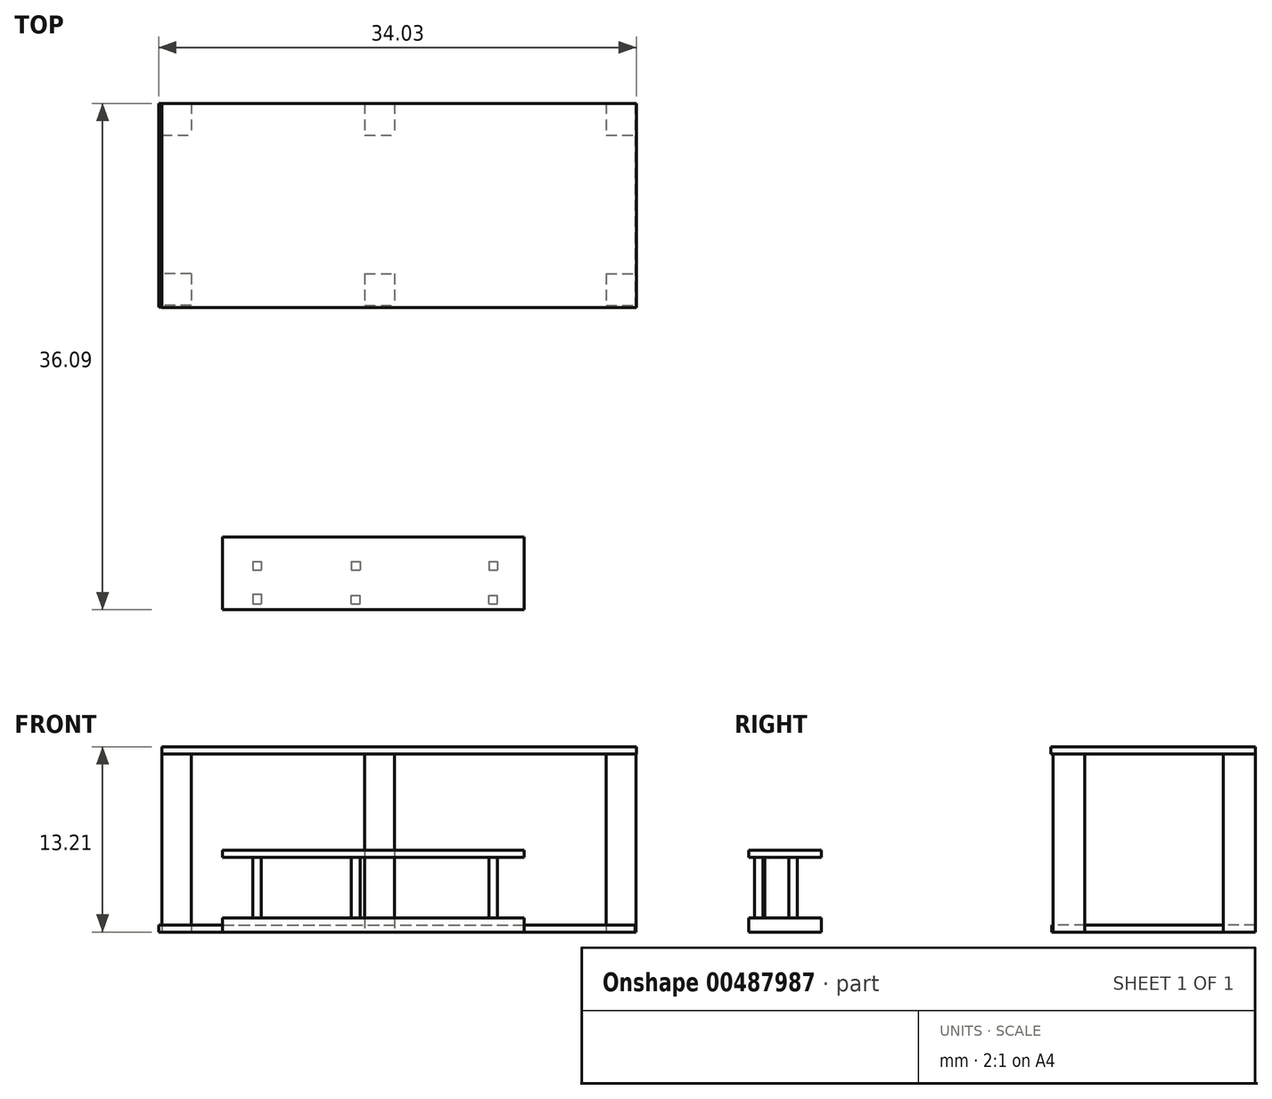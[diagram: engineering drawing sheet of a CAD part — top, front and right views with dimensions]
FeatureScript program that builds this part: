
annotation { "Feature Type Name" : "Feature", "Feature Type Description" : "" }
export const myFeature = defineFeature(function(context is Context, id is Id, definition is map)
    precondition{}
    {
        {
            var Q0;
            Q0=qCreatedBy(makeId("Top.planeOp"),FACE);
            var sketch = newSketch(context, id + "F0", { "sketchPlane" : qUnion([Q0])});
            skLineSegment(sketch, "E0.bottom", {"start": v(20.7, -5.96) * mm, "end": v(-20.7, -5.96) * mm});
            skLineSegment(sketch, "E0.top", {"start": v(20.7, 5.96) * mm, "end": v(-20.7, 5.96) * mm});
            skLineSegment(sketch, "E0.left", {"start": v(20.7, -5.96) * mm, "end": v(20.7, 5.96) * mm});
            skLineSegment(sketch, "E0.right", {"start": v(-20.7, -5.96) * mm, "end": v(-20.7, 5.96) * mm});
            skPoint(sketch, "E0.middle", {"position": v(0, 0) * mm});
            skPoint(sketch, "E1.middle", {"position": v(0, -5.96) * mm});
            skPoint(sketch, "E2.middle", {"position": v(-2.45, -5.96) * mm});
            skLineSegment(sketch, "E3.bottom", {"start": v(-2.45, -5.96) * mm, "end": v(0, -5.96) * mm});
            skLineSegment(sketch, "E3.top", {"start": v(-2.45, -23.4) * mm, "end": v(0, -23.4) * mm});
            skLineSegment(sketch, "E3.left", {"start": v(-2.45, -5.96) * mm, "end": v(-2.45, -23.4) * mm});
            skLineSegment(sketch, "E3.right", {"start": v(0, -5.96) * mm, "end": v(0, -23.4) * mm});
            skLineSegment(sketch, "E4.bottom", {"start": v(9.25, -23.4) * mm, "end": v(-12.25, -23.4) * mm});
            skLineSegment(sketch, "E4.top", {"start": v(9.25, -23.4) * mm, "end": v(-12.25, -23.4) * mm});
            skLineSegment(sketch, "E4.left", {"start": v(9.25, -23.4) * mm, "end": v(9.25, -23.4) * mm});
            skLineSegment(sketch, "E4.right", {"start": v(-12.25, -23.4) * mm, "end": v(-12.25, -23.4) * mm});
            skLineSegment(sketch, "E5", {"start": v(-12.25, -23.4) * mm, "end": v(-12.25, -28.58) * mm});
            skLineSegment(sketch, "E6", {"start": v(-12.25, -28.58) * mm, "end": v(9.25, -28.58) * mm});
            skLineSegment(sketch, "E7", {"start": v(9.25, -28.58) * mm, "end": v(9.25, -23.4) * mm});
            skSolve(sketch);
        }
        {
            var Q0;
            Q0=qCreatedBy(makeId("Top.planeOp"),FACE);
            var sketch = newSketch(context, id + "F1", { "sketchPlane" : qUnion([Q0])});
            skLineSegment(sketch, "E8.bottom", {"start": v(-16.58, 7.51) * mm, "end": v(-14.47, 7.51) * mm});
            skLineSegment(sketch, "E8.top", {"start": v(-16.58, 5.25) * mm, "end": v(-14.47, 5.25) * mm});
            skLineSegment(sketch, "E8.left", {"start": v(-16.58, 7.51) * mm, "end": v(-16.58, 5.25) * mm});
            skLineSegment(sketch, "E8.right", {"start": v(-14.47, 7.51) * mm, "end": v(-14.47, 5.25) * mm});
            skLineSegment(sketch, "E9.bottom", {"start": v(-14.47, -4.62) * mm, "end": v(-16.58, -4.62) * mm});
            skLineSegment(sketch, "E9.top", {"start": v(-14.47, -6.88) * mm, "end": v(-16.58, -6.88) * mm});
            skLineSegment(sketch, "E9.left", {"start": v(-14.47, -4.62) * mm, "end": v(-14.47, -6.88) * mm});
            skLineSegment(sketch, "E9.right", {"start": v(-16.58, -4.62) * mm, "end": v(-16.58, -6.88) * mm});
            skLineSegment(sketch, "E10.bottom", {"start": v(-2.1, 7.51) * mm, "end": v(0, 7.51) * mm});
            skLineSegment(sketch, "E10.top", {"start": v(-2.1, 5.25) * mm, "end": v(0, 5.25) * mm});
            skLineSegment(sketch, "E10.left", {"start": v(-2.1, 7.51) * mm, "end": v(-2.1, 5.25) * mm});
            skLineSegment(sketch, "E10.right", {"start": v(0, 7.51) * mm, "end": v(0, 5.25) * mm});
            skLineSegment(sketch, "E11.bottom", {"start": v(-2.1, -4.62) * mm, "end": v(0, -4.62) * mm});
            skLineSegment(sketch, "E11.top", {"start": v(-2.1, -6.88) * mm, "end": v(0, -6.88) * mm});
            skLineSegment(sketch, "E11.left", {"start": v(-2.1, -4.62) * mm, "end": v(-2.1, -6.88) * mm});
            skLineSegment(sketch, "E11.right", {"start": v(0, -4.62) * mm, "end": v(0, -6.88) * mm});
            skLineSegment(sketch, "E12.bottom", {"start": v(15.1, 7.51) * mm, "end": v(17.2, 7.51) * mm});
            skLineSegment(sketch, "E12.top", {"start": v(15.1, 5.25) * mm, "end": v(17.2, 5.25) * mm});
            skLineSegment(sketch, "E12.left", {"start": v(15.1, 7.51) * mm, "end": v(15.1, 5.25) * mm});
            skLineSegment(sketch, "E12.right", {"start": v(17.2, 7.51) * mm, "end": v(17.2, 5.25) * mm});
            skLineSegment(sketch, "E13.bottom", {"start": v(15.1, -4.62) * mm, "end": v(17.2, -4.62) * mm});
            skLineSegment(sketch, "E13.top", {"start": v(15.1, -6.88) * mm, "end": v(17.2, -6.88) * mm});
            skLineSegment(sketch, "E13.left", {"start": v(15.1, -4.62) * mm, "end": v(15.1, -6.88) * mm});
            skLineSegment(sketch, "E13.right", {"start": v(17.2, -4.62) * mm, "end": v(17.2, -6.88) * mm});
            skSolve(sketch);
        }
        {
            var Q0;
            Q0 = qSketchRegion(id + "F1", true);
            extrude(context, id + "F2", {"entities" : qUnion([Q0]), "depth" : 12.7 * mm});
        }
        {
            var Q0;
            Q0=makeQuery(id+"F6QYhZ10MttGIGM_6.imprint","IMPRINT",FACE,{"disambiguationData":[TD([[makeQuery(id+"F6QYhZ10MttGIGM_6.imprint","IMPRINT",EDGE,{"derivedFrom":sQuery(id+"F6QYhZ10MttGIGM_6.wireOp",EDGE,"uMPXpFjo-ONPb-R2jX-ZlyI-16el99lNTxus.bottom")}),-1.0]])]});
            var Q1;
            Q1=makeQuery(id+"F0.imprint","IMPRINT",FACE,{"disambiguationData":[TD([[makeQuery(id+"F0.imprint","IMPRINT",EDGE,{"derivedFrom":sQuery(id+"F0.wireOp",EDGE,"E3.bottom")}),-1.0]])]});
            var Q2;
            {var subQ0=sQuery(id+"F0.wireOp",EDGE,"E5");Q2=makeQuery(id+"F0.imprint","IMPRINT",FACE,{"disambiguationData":[TD([[makeQuery(id+"F0.imprint","IMPRINT",EDGE,{"derivedFrom":subQ0}),1.0]])]});}
            extrude(context, id + "F3", {"entities" : qUnion([Q0, Q1, Q2]), "depth" : 1.02 * mm});
        }
        {
            var Q0;
            Q0=makeQuery(id+"F3.opExtrude","CAP_FACE",FACE,{"disambiguationData":[OSD([sQuery(id+"F0.wireOp",EDGE,"E3.bottom"),sQuery(id+"F0.wireOp",EDGE,"E3.left"),sQuery(id+"F0.wireOp",EDGE,"E3.right"),sQuery(id+"F0.wireOp",EDGE,"E4.top"),sQuery(id+"F0.wireOp",EDGE,"E5"),sQuery(id+"F0.wireOp",EDGE,"E6"),sQuery(id+"F0.wireOp",EDGE,"E7")])],"isStart":false});
            var sketch = newSketch(context, id + "F4", { "sketchPlane" : qUnion([Q0])});
            skLineSegment(sketch, "E14.bottom", {"start": v(-10.09, -25.12) * mm, "end": v(-9.48, -25.12) * mm});
            skLineSegment(sketch, "E14.top", {"start": v(-10.09, -25.72) * mm, "end": v(-9.48, -25.72) * mm});
            skLineSegment(sketch, "E14.left", {"start": v(-10.09, -25.12) * mm, "end": v(-10.09, -25.72) * mm});
            skLineSegment(sketch, "E14.right", {"start": v(-9.48, -25.12) * mm, "end": v(-9.48, -25.72) * mm});
            skLineSegment(sketch, "E15.bottom", {"start": v(-10.09, -27.45) * mm, "end": v(-9.48, -27.45) * mm});
            skLineSegment(sketch, "E15.top", {"start": v(-10.09, -28.16) * mm, "end": v(-9.48, -28.16) * mm});
            skLineSegment(sketch, "E15.left", {"start": v(-10.09, -27.45) * mm, "end": v(-10.09, -28.16) * mm});
            skLineSegment(sketch, "E15.right", {"start": v(-9.48, -27.45) * mm, "end": v(-9.48, -28.16) * mm});
            skLineSegment(sketch, "E16.bottom", {"start": v(-3.06, -25.12) * mm, "end": v(-2.45, -25.12) * mm});
            skLineSegment(sketch, "E16.top", {"start": v(-3.06, -25.72) * mm, "end": v(-2.45, -25.72) * mm});
            skLineSegment(sketch, "E16.left", {"start": v(-3.06, -25.12) * mm, "end": v(-3.06, -25.72) * mm});
            skLineSegment(sketch, "E16.right", {"start": v(-2.45, -25.12) * mm, "end": v(-2.45, -25.72) * mm});
            skLineSegment(sketch, "E17.bottom", {"start": v(-3.06, -28.16) * mm, "end": v(-2.45, -28.16) * mm});
            skLineSegment(sketch, "E17.top", {"start": v(-3.06, -27.55) * mm, "end": v(-2.45, -27.55) * mm});
            skLineSegment(sketch, "E17.left", {"start": v(-3.06, -28.16) * mm, "end": v(-3.06, -27.55) * mm});
            skLineSegment(sketch, "E17.right", {"start": v(-2.45, -28.16) * mm, "end": v(-2.45, -27.55) * mm});
            skLineSegment(sketch, "E18.bottom", {"start": v(6.74, -25.12) * mm, "end": v(7.34, -25.12) * mm});
            skLineSegment(sketch, "E18.top", {"start": v(6.74, -25.72) * mm, "end": v(7.34, -25.72) * mm});
            skLineSegment(sketch, "E18.left", {"start": v(6.74, -25.12) * mm, "end": v(6.74, -25.72) * mm});
            skLineSegment(sketch, "E18.right", {"start": v(7.34, -25.12) * mm, "end": v(7.34, -25.72) * mm});
            skLineSegment(sketch, "E19.bottom", {"start": v(6.74, -28.16) * mm, "end": v(7.34, -28.16) * mm});
            skLineSegment(sketch, "E19.top", {"start": v(6.74, -27.55) * mm, "end": v(7.34, -27.55) * mm});
            skLineSegment(sketch, "E19.left", {"start": v(6.74, -28.16) * mm, "end": v(6.74, -27.55) * mm});
            skLineSegment(sketch, "E19.right", {"start": v(7.34, -28.16) * mm, "end": v(7.34, -27.55) * mm});
            skSolve(sketch);
        }
        {
            var Q0;
            Q0=makeQuery(id+"F4.imprint","IMPRINT",FACE,{"disambiguationData":[TD([[makeQuery(id+"F4.imprint","IMPRINT",EDGE,{"derivedFrom":sQuery(id+"F4.wireOp",EDGE,"E14.bottom")}),-1.0]])]});
            var Q1;
            Q1=makeQuery(id+"F4.imprint","IMPRINT",FACE,{"disambiguationData":[TD([[makeQuery(id+"F4.imprint","IMPRINT",EDGE,{"derivedFrom":sQuery(id+"F4.wireOp",EDGE,"E15.bottom")}),-1.0]])]});
            var Q2;
            Q2=makeQuery(id+"F4.imprint","IMPRINT",FACE,{"disambiguationData":[TD([[makeQuery(id+"F4.imprint","IMPRINT",EDGE,{"derivedFrom":sQuery(id+"F4.wireOp",EDGE,"E16.bottom")}),-1.0]])]});
            var Q3;
            Q3=makeQuery(id+"F4.imprint","IMPRINT",FACE,{"disambiguationData":[TD([[makeQuery(id+"F4.imprint","IMPRINT",EDGE,{"derivedFrom":sQuery(id+"F4.wireOp",EDGE,"E17.bottom")}),1.0]])]});
            var Q4;
            Q4=makeQuery(id+"F4.imprint","IMPRINT",FACE,{"disambiguationData":[TD([[makeQuery(id+"F4.imprint","IMPRINT",EDGE,{"derivedFrom":sQuery(id+"F4.wireOp",EDGE,"E18.bottom")}),-1.0]])]});
            var Q5;
            Q5=makeQuery(id+"F4.imprint","IMPRINT",FACE,{"disambiguationData":[TD([[makeQuery(id+"F4.imprint","IMPRINT",EDGE,{"derivedFrom":sQuery(id+"F4.wireOp",EDGE,"E19.bottom")}),1.0]])]});
            extrude(context, id + "F5", {"entities" : qUnion([Q0, Q1, Q2, Q3, Q4, Q5]), "operationType" : NewBodyOperationType.ADD, "depth" : 4.32 * mm});
        }
        {
            var Q0;
            Q0=makeQuery(id+"F5.opExtrude","CAP_FACE",FACE,{"disambiguationData":[OSD([sQuery(id+"F4.wireOp",EDGE,"E14.bottom"),sQuery(id+"F4.wireOp",EDGE,"E14.top"),sQuery(id+"F4.wireOp",EDGE,"E14.left"),sQuery(id+"F4.wireOp",EDGE,"E14.right")])],"isStart":false});
            var sketch = newSketch(context, id + "F6", { "sketchPlane" : qUnion([Q0])});
            skLineSegment(sketch, "E20.bottom", {"start": v(-12.24, -23.4) * mm, "end": v(9.25, -23.4) * mm});
            skLineSegment(sketch, "E20.top", {"start": v(-12.24, -28.58) * mm, "end": v(9.25, -28.58) * mm});
            skLineSegment(sketch, "E20.left", {"start": v(-12.24, -23.4) * mm, "end": v(-12.24, -28.58) * mm});
            skLineSegment(sketch, "E20.right", {"start": v(9.25, -23.4) * mm, "end": v(9.25, -28.58) * mm});
            skSolve(sketch);
        }
        {
            var Q0;
            Q0=makeQuery(id+"F6.imprint","IMPRINT",FACE,{"disambiguationData":[TD([[makeQuery(id+"F6.imprint","IMPRINT",EDGE,{"derivedFrom":sQuery(id+"F6.wireOp",EDGE,"E20.bottom")}),-1.0]])]});
            var Q1;
            Q1=makeQuery(id+"F6.imprint","IMPRINT",FACE,{"disambiguationData":[TD([[makeQuery(id+"F6.imprint","IMPRINT",EDGE,{"derivedFrom":makeQuery(id+"F5.opExtrude","CAP_EDGE",EDGE,{"disambiguationData":[OSD([sQuery(id+"F4.wireOp",EDGE,"E14.bottom")])],"isStart":false})}),-1.0]])]});
            extrude(context, id + "F7", {"entities" : qUnion([Q0, Q1]), "depth" : 0.5 * mm});
        }
        {
            var Q0;
            Q0=qCreatedBy(makeId("Top.planeOp"),FACE);
            var sketch = newSketch(context, id + "F8", { "sketchPlane" : qUnion([Q0])});
            skLineSegment(sketch, "E21.bottom", {"start": v(-16.79, 7.5) * mm, "end": v(17.16, 7.5) * mm});
            skLineSegment(sketch, "E21.top", {"start": v(-16.79, -7) * mm, "end": v(17.16, -7) * mm});
            skLineSegment(sketch, "E21.left", {"start": v(-16.79, 7.5) * mm, "end": v(-16.79, -7) * mm});
            skLineSegment(sketch, "E21.right", {"start": v(17.16, 7.5) * mm, "end": v(17.16, -7) * mm});
            skSolve(sketch);
        }
        {
            var Q0;
            Q0=makeQuery(id+"F8.imprint","IMPRINT",FACE,{"disambiguationData":[TD([[makeQuery(id+"F8.imprint","IMPRINT",EDGE,{"derivedFrom":sQuery(id+"F8.wireOp",EDGE,"E21.bottom")}),-1.0]])]});
            extrude(context, id + "F9", {"entities" : qUnion([Q0]), "depth" : 0.5 * mm});
        }
        {
            var Q0;
            Q0=makeQuery(id+"F2.opExtrude","CAP_FACE",FACE,{"disambiguationData":[OSD([sQuery(id+"F1.wireOp",EDGE,"E8.bottom"),sQuery(id+"F1.wireOp",EDGE,"E8.top"),sQuery(id+"F1.wireOp",EDGE,"E8.left"),sQuery(id+"F1.wireOp",EDGE,"E8.right")])],"isStart":false});
            var sketch = newSketch(context, id + "F10", { "sketchPlane" : qUnion([Q0])});
            skLineSegment(sketch, "E22.bottom", {"start": v(-16.58, 7.51) * mm, "end": v(17.24, 7.51) * mm});
            skLineSegment(sketch, "E22.top", {"start": v(-16.58, -7.04) * mm, "end": v(17.24, -7.04) * mm});
            skLineSegment(sketch, "E22.left", {"start": v(-16.58, 7.51) * mm, "end": v(-16.58, -7.04) * mm});
            skLineSegment(sketch, "E22.right", {"start": v(17.24, 7.51) * mm, "end": v(17.24, -7.04) * mm});
            skSolve(sketch);
        }
        {
            var Q0;
            {var subQ2=sQuery(id+"F10.wireOp",EDGE,"E22.top");Q0=makeQuery(id+"F10.imprint","IMPRINT",FACE,{"disambiguationData":[TD([[makeQuery(id+"F10.imprint","IMPRINT",EDGE,{"derivedFrom":subQ2}),1.0]])]});}
            var Q1;
            {var subQ4=makeQuery(id+"F2.opExtrude","CAP_EDGE",EDGE,{"disambiguationData":[OSD([sQuery(id+"F1.wireOp",EDGE,"E8.top")])],"isStart":false});Q1=makeQuery(id+"F10.imprint","IMPRINT",FACE,{"disambiguationData":[TD([[makeQuery(id+"F10.imprint","IMPRINT",EDGE,{"derivedFrom":subQ4}),1.0]])]});}
            extrude(context, id + "F11", {"entities" : qUnion([Q0, Q1]), "depth" : 0.5 * mm});
        }
    });
